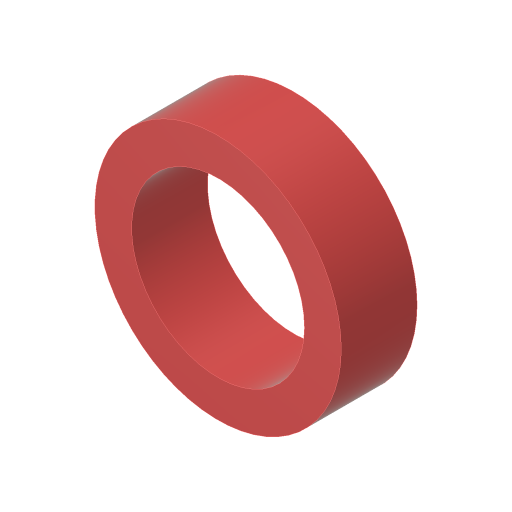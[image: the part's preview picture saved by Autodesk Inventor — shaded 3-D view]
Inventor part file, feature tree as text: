
AUTODESK INVENTOR PART (.ipt)
format: ipt  version: 2023.4 (Build 274418000, 418)  size: 114,688 bytes
history: native  units: in
note: dims shown in document units (in); Inventor stores cm internally (conversion verified against a paired STEP export)
features: extrude x1, sketch x1
ambient origin geometry x8: Origin, YZ Plane, XZ Plane, XY Plane, X Axis, Y Axis, Z Axis, Center Point
bodies: Solid1 (feature_tree)
feature tree (2):
  extrude  "Extrusion1"  Depth=0.257in
  sketch  "Sketch1"  dims[d0=0.585in d1=0.125in d2=0.257in d3=0.0in]
